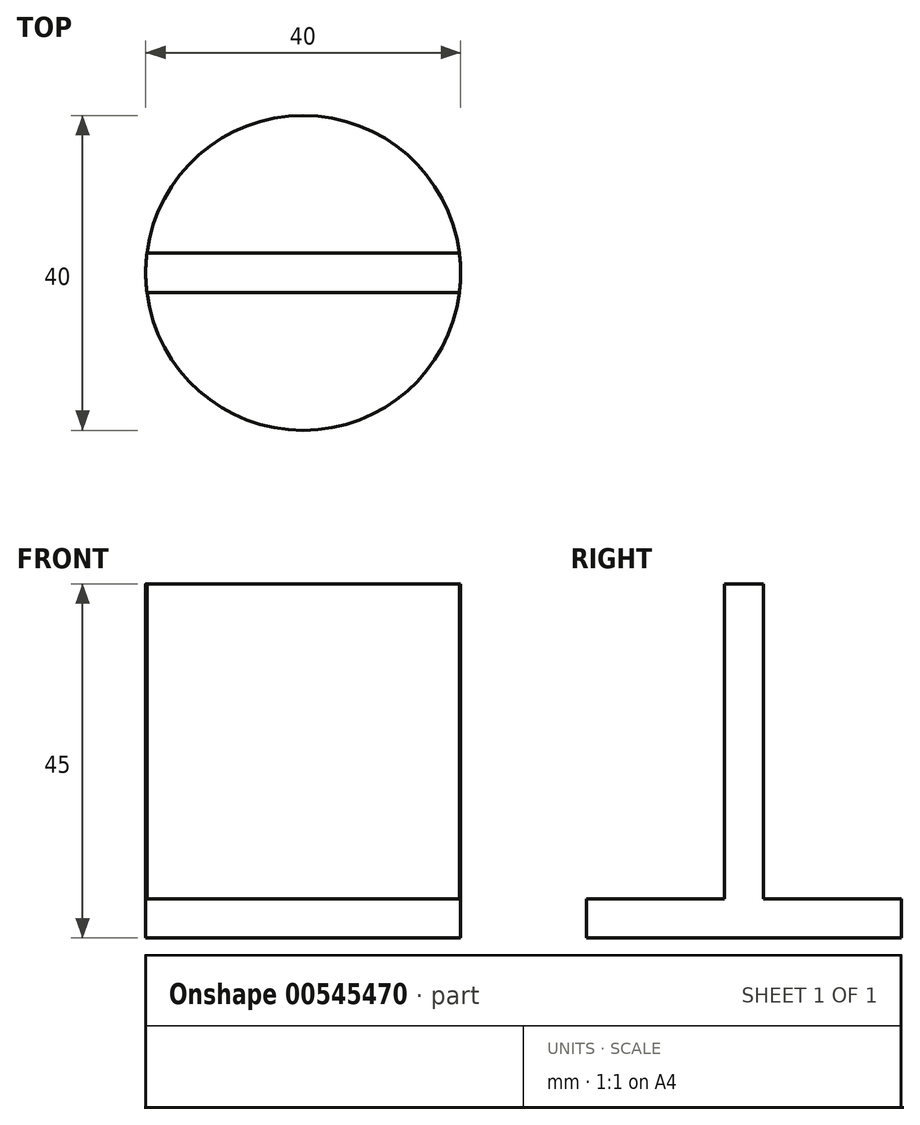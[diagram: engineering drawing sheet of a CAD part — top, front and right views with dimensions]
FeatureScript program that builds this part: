
annotation { "Feature Type Name" : "Feature", "Feature Type Description" : "" }
export const myFeature = defineFeature(function(context is Context, id is Id, definition is map)
    precondition{}
    {
        {
            var Q0;
            Q0=qCreatedBy(makeId("Top.planeOp"),FACE);
            var sketch = newSketch(context, id + "F0", { "sketchPlane" : qUnion([Q0])});
            skCircle(sketch, "E0", {"center": v(0, 0) * mm, "radius": 20 * mm});
            skSolve(sketch);
        }
        {
            var Q0;
            Q0=makeQuery(id+"F0.imprint","IMPRINT",FACE,{"disambiguationData":[TD([[makeQuery(id+"F0.imprint","IMPRINT",EDGE,{"derivedFrom":sQuery(id+"F0.wireOp",EDGE,"E0")}),1.0]])]});
            extrude(context, id + "F1", {"entities" : qUnion([Q0]), "depth" : 5 * mm, "offsetDistance" : 25 * mm});
        }
        {
            var Q0;
            Q0=makeQuery(id+"F1.opExtrude","CAP_FACE",FACE,{"disambiguationData":[OSD([sQuery(id+"F0.wireOp",EDGE,"E0")])],"isStart":false});
            var sketch = newSketch(context, id + "F2", { "sketchPlane" : qUnion([Q0])});
            skArc(sketch, "E1", {"start": v(-19.84, 2.5) * mm, "mid": v(-20, 0) * mm, "end": v(-19.84, -2.5) * mm});
            skLineSegment(sketch, "E2", {"start": v(-19.84, -2.5) * mm, "end": v(19.84, -2.5) * mm});
            skLineSegment(sketch, "E3.MirrorCS", {"start": v(-19.84, 2.5) * mm, "end": v(19.84, 2.5) * mm});
            skPoint(sketch, "E4.orphan", {"position": v(-33.5, -2.5) * mm});
            skPoint(sketch, "E5.orphan", {"position": v(-33.5, 2.5) * mm});
            skPoint(sketch, "E6.orphan", {"position": v(50.7, 2.5) * mm});
            skPoint(sketch, "E7.orphan", {"position": v(50.7, -2.5) * mm});
            skArc(sketch, "E8.trimOffspring", {"start": v(19.84, -2.5) * mm, "mid": v(20, 0) * mm, "end": v(19.84, 2.5) * mm});
            skSolve(sketch);
        }
        {
            var Q0;
            Q0=makeQuery(id+"F2.imprint","IMPRINT",FACE,{"disambiguationData":[TD([[makeQuery(id+"F2.imprint","IMPRINT",EDGE,{"derivedFrom":sQuery(id+"F2.wireOp",EDGE,"E2")}),1.0]])]});
            extrude(context, id + "F3", {"entities" : qUnion([Q0]), "operationType" : NewBodyOperationType.ADD, "depth" : 40 * mm, "offsetDistance" : 25 * mm});
        }
    });
